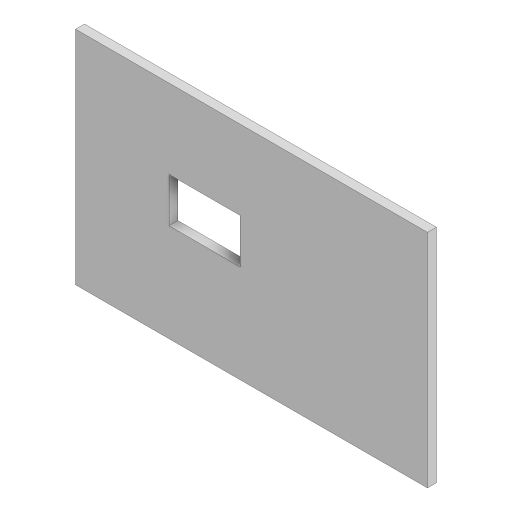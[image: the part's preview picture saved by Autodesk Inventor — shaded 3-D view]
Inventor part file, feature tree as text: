
AUTODESK INVENTOR PART (.ipt)
format: ipt  version: 2024.1 (Build 281209000, 209)  size: 207,360 bytes
history: native  units: in
note: dims shown in document units (in); Inventor stores cm internally (conversion verified against a paired STEP export)
features: extrude x1, sketch x1
ambient origin geometry x8: Origin, YZ Plane, XZ Plane, XY Plane, X Axis, Y Axis, Z Axis, Center Point
bodies: Solid1 (feature_tree)
feature tree (2):
  extrude  "Extrusion1"  Depth=1.9685in
  sketch  "Sketch1"  dims[d0=3.1496in d1=1.9685in d2=0.3937in d3=0.0in d4=4.1339in d5=4.3307in]
